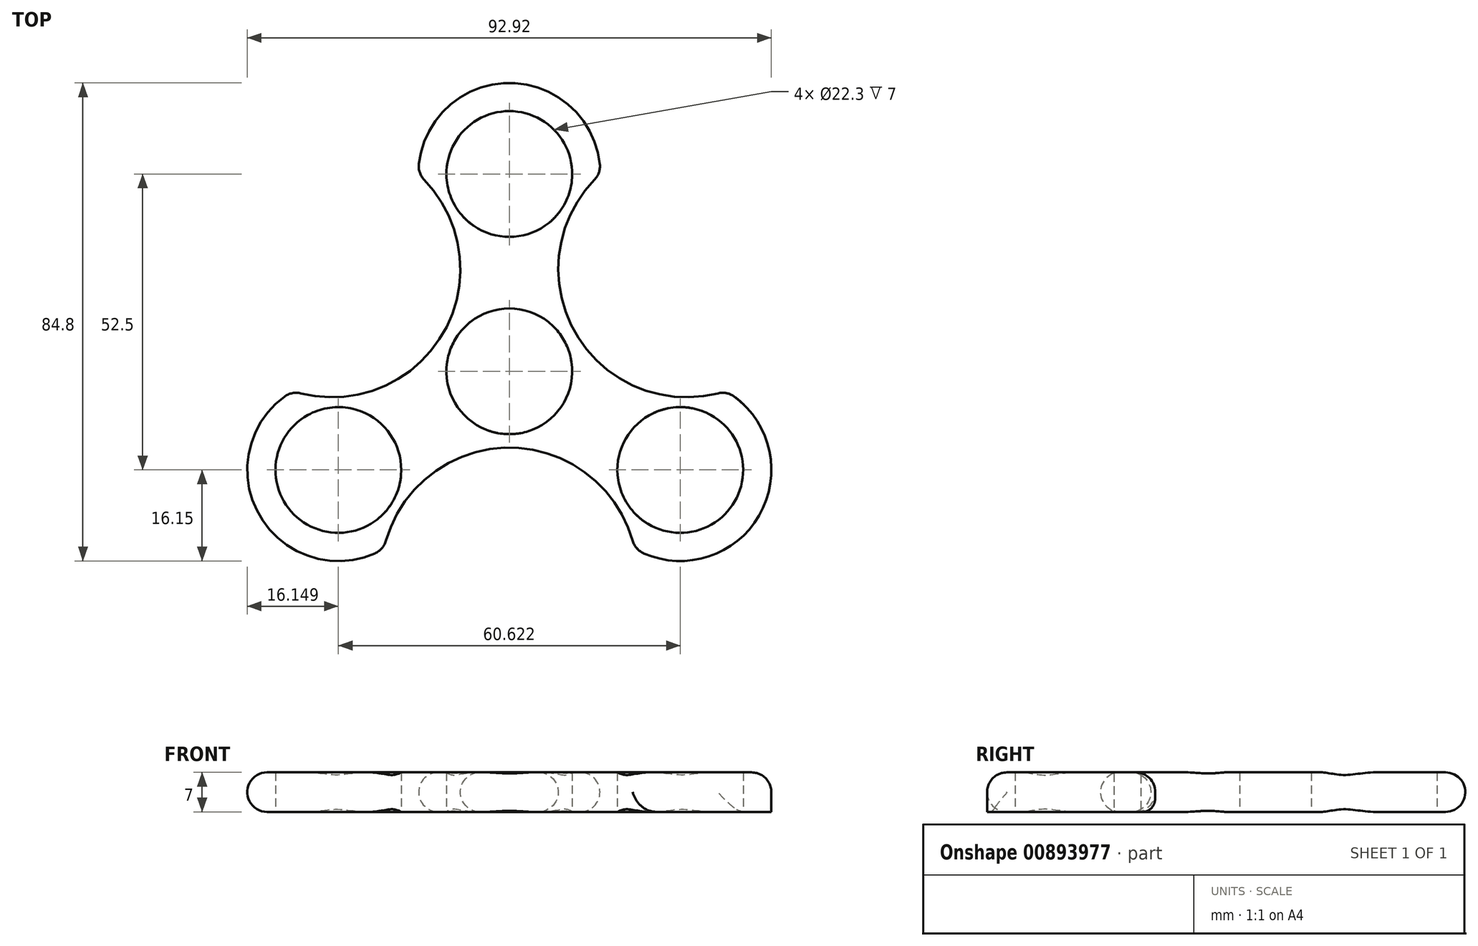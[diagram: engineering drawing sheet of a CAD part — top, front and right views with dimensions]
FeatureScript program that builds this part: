
annotation { "Feature Type Name" : "Feature", "Feature Type Description" : "" }
export const myFeature = defineFeature(function(context is Context, id is Id, definition is map)
    precondition{}
    {
        {
            var Q0;
            Q0=qCreatedBy(makeId("Top.planeOp"),FACE);
            var sketch = newSketch(context, id + "F0", { "sketchPlane" : qUnion([Q0])});
            skCircle(sketch, "E0", {"center": v(0, 0) * mm, "radius": 11.15 * mm});
            skLineSegment(sketch, "E1", {"start": v(0, 0) * mm, "end": v(0, 35) * mm, "construction": true});
            skCircle(sketch, "E2", {"center": v(0, 35) * mm, "radius": 11.15 * mm});
            skCircle(sketch, "E3.1.0", {"center": v(-30.31, -17.5) * mm, "radius": 11.15 * mm});
            skCircle(sketch, "E3.2.0", {"center": v(30.31, -17.5) * mm, "radius": 11.15 * mm});
            skArc(sketch, "E4.0", {"start": v(16.15, 35) * mm, "mid": v(0, 51.15) * mm, "end": v(-16.15, 35) * mm});
            skArc(sketch, "E5.0", {"start": v(22.24, -31.49) * mm, "mid": v(44.3, -25.58) * mm, "end": v(38.39, -3.51) * mm});
            skArc(sketch, "E6.0", {"start": v(-38.39, -3.51) * mm, "mid": v(-44.3, -25.57) * mm, "end": v(-22.24, -31.49) * mm});
            skLineSegment(sketch, "E7", {"start": v(0, 35) * mm, "end": v(16.15, 35) * mm, "construction": true});
            skLineSegment(sketch, "E8", {"start": v(0, 35) * mm, "end": v(0, 18.85) * mm, "construction": true});
            skLineSegment(sketch, "E9", {"start": v(0, 0) * mm, "end": v(30.31, -17.5) * mm, "construction": true});
            skLineSegment(sketch, "E10", {"start": v(30.31, -17.5) * mm, "end": v(39.19, -2.13) * mm, "construction": true});
            skArc(sketch, "E11", {"start": v(16.15, 35) * mm, "mid": v(11.73, 6.77) * mm, "end": v(38.39, -3.51) * mm});
            skArc(sketch, "E12.1.0", {"start": v(-38.39, -3.51) * mm, "mid": v(-11.73, 6.77) * mm, "end": v(-16.15, 35) * mm});
            skArc(sketch, "E12.2.0", {"start": v(22.24, -31.49) * mm, "mid": v(0, -13.54) * mm, "end": v(-22.24, -31.49) * mm});
            skSolve(sketch);
        }
        {
            var Q0;
            Q0=makeQuery(id+"F0.imprint","IMPRINT",FACE,{"disambiguationData":[TD([[makeQuery(id+"F0.imprint","IMPRINT",EDGE,{"derivedFrom":sQuery(id+"F0.wireOp",EDGE,"E0")}),-1.0]])]});
            extrude(context, id + "F1", {"entities" : qUnion([Q0]), "depth" : 7 * mm, "offsetDistance" : 25 * mm});
        }
        {
            var Q0;
            Q0=makeQuery(id+"F1.opExtrude","SWEPT_FACE",FACE,{"disambiguationData":[OSD([sQuery(id+"F0.wireOp",EDGE,"E12.2.0")])]});
            var Q1;
            Q1=makeQuery(id+"F1.opExtrude","SWEPT_FACE",FACE,{"disambiguationData":[OSD([sQuery(id+"F0.wireOp",EDGE,"E6.0")])]});
            var Q2;
            Q2=makeQuery(id+"F1.opExtrude","SWEPT_FACE",FACE,{"disambiguationData":[OSD([sQuery(id+"F0.wireOp",EDGE,"E12.1.0")])]});
            var Q3;
            Q3=makeQuery(id+"F1.opExtrude","SWEPT_FACE",FACE,{"disambiguationData":[OSD([sQuery(id+"F0.wireOp",EDGE,"E4.0")])]});
            var Q4;
            Q4=makeQuery(id+"F1.opExtrude","SWEPT_FACE",FACE,{"disambiguationData":[OSD([sQuery(id+"F0.wireOp",EDGE,"E11")])]});
            var Q5;
            Q5=makeQuery(id+"F1.opExtrude","CAP_EDGE",EDGE,{"disambiguationData":[OSD([sQuery(id+"F0.wireOp",EDGE,"E5.0")])],"isStart":false});
            fillet(context, id + "F2", {"entities" : qUnion([Q0, Q1, Q2, Q3, Q4, Q5]), "radius" : 3.5 * mm, "tangentPropagation" : true, "allowEdgeOverflow" : false});
        }
    });
